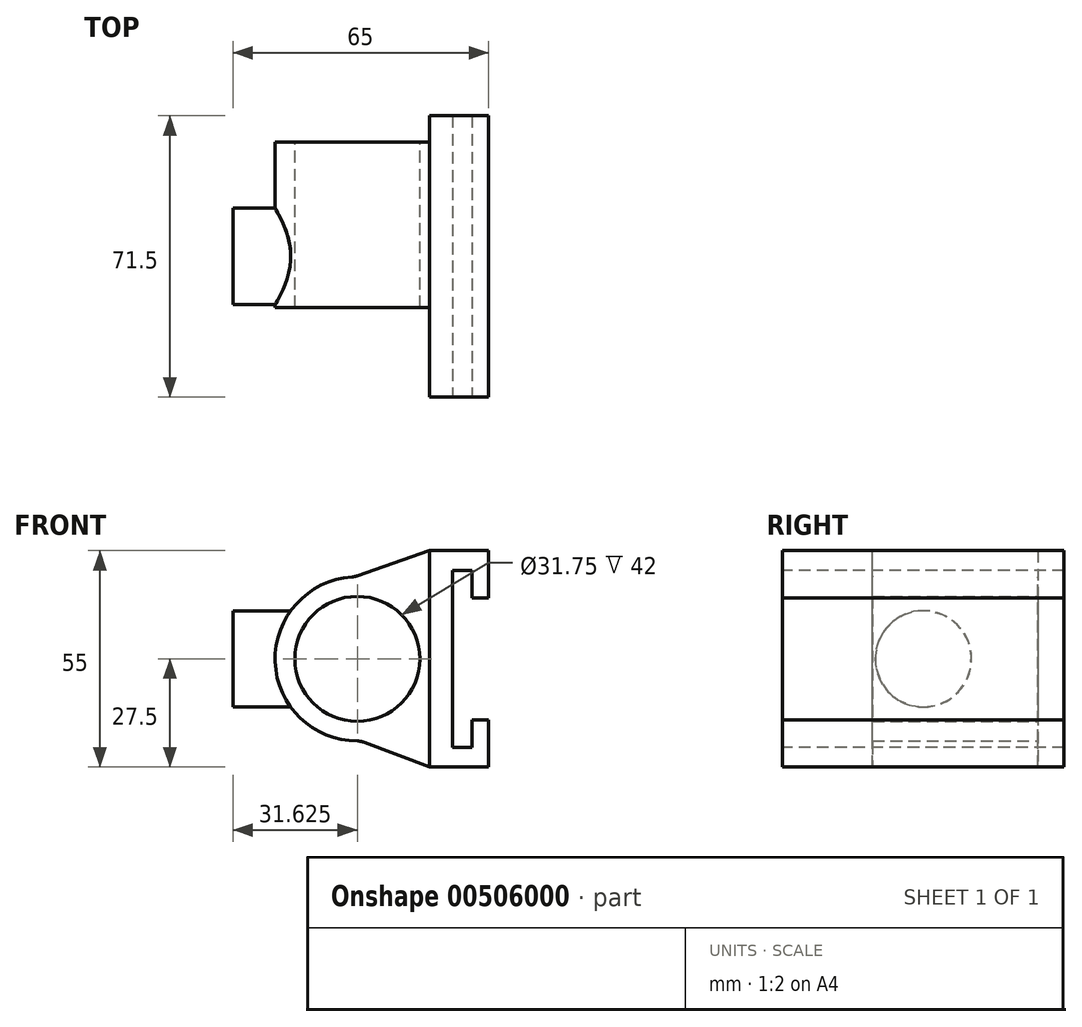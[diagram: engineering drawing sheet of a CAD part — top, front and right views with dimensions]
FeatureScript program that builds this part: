
annotation { "Feature Type Name" : "Feature", "Feature Type Description" : "" }
export const myFeature = defineFeature(function(context is Context, id is Id, definition is map)
    precondition{}
    {
        {
            var Q0;
            Q0=qCreatedBy(makeId("Front.planeOp"),FACE);
            var sketch = newSketch(context, id + "F0", { "sketchPlane" : qUnion([Q0])});
            skLineSegment(sketch, "E0", {"start": v(0, 0) * mm, "end": v(0, 7) * mm});
            skLineSegment(sketch, "E1", {"start": v(0, 0) * mm, "end": v(4.25, 0) * mm});
            skLineSegment(sketch, "E2", {"start": v(4.25, 0) * mm, "end": v(4.25, 12) * mm});
            skLineSegment(sketch, "E3", {"start": v(4.25, 12) * mm, "end": v(-10.75, 12) * mm});
            skLineSegment(sketch, "E4", {"start": v(-10.75, 12) * mm, "end": v(-10.75, -30) * mm});
            skLineSegment(sketch, "E5", {"start": v(-10.75, 12) * mm, "end": v(-10.75, -9) * mm});
            skLineSegment(sketch, "E6.MirrorCS", {"start": v(4.25, -43) * mm, "end": v(-10.75, -43) * mm});
            skLineSegment(sketch, "E7.MirrorCS", {"start": v(0, -31) * mm, "end": v(4.25, -31) * mm});
            skLineSegment(sketch, "E8.MirrorCS", {"start": v(4.25, -31) * mm, "end": v(4.25, -43) * mm});
            skLineSegment(sketch, "E9", {"start": v(-4, -25) * mm, "end": v(-4, 7) * mm});
            skLineSegment(sketch, "E10", {"start": v(-4, 7) * mm, "end": v(0, 7) * mm});
            skLineSegment(sketch, "E11", {"start": v(-10.75, -30) * mm, "end": v(-10.75, -43) * mm});
            skLineSegment(sketch, "E12", {"start": v(-4, -25) * mm, "end": v(-4, -31) * mm});
            skLineSegment(sketch, "E13", {"start": v(0, -31) * mm, "end": v(0, -38) * mm});
            skLineSegment(sketch, "E14", {"start": v(0, -38) * mm, "end": v(-4, -38) * mm});
            skLineSegment(sketch, "E15", {"start": v(-4, -38) * mm, "end": v(-4, -31) * mm});
            skSolve(sketch);
        }
        {
            var Q0;
            Q0 = qSketchRegion(id + "F0", true);
            extrude(context, id + "F1", {"entities" : qUnion([Q0]), "depth" : 71.5 * mm, "offsetDistance" : 25 * mm});
        }
        {
            var Q0;
            Q0=makeQuery(id+"F1.opExtrude","CAP_FACE",FACE,{"disambiguationData":[OSD([sQuery(id+"F0.wireOp",EDGE,"E0"),sQuery(id+"F0.wireOp",EDGE,"E1"),sQuery(id+"F0.wireOp",EDGE,"E2"),sQuery(id+"F0.wireOp",EDGE,"E3"),sQuery(id+"F0.wireOp",EDGE,"E4"),sQuery(id+"F0.wireOp",EDGE,"E5"),sQuery(id+"F0.wireOp",EDGE,"E6.MirrorCS"),sQuery(id+"F0.wireOp",EDGE,"E7.MirrorCS"),sQuery(id+"F0.wireOp",EDGE,"E8.MirrorCS"),sQuery(id+"F0.wireOp",EDGE,"E9"),sQuery(id+"F0.wireOp",EDGE,"E10"),sQuery(id+"F0.wireOp",EDGE,"E11"),sQuery(id+"F0.wireOp",EDGE,"E12"),sQuery(id+"F0.wireOp",EDGE,"E13"),sQuery(id+"F0.wireOp",EDGE,"E14"),sQuery(id+"F0.wireOp",EDGE,"E15")])],"isStart":false});
            var sketch = newSketch(context, id + "F2", { "sketchPlane" : qUnion([Q0])});
            skLineSegment(sketch, "E16", {"start": v(-10.75, -15.5) * mm, "end": v(-13.25, -15.5) * mm});
            skPoint(sketch, "E16.endSnap0", {"position": v(-10.75, -15.5) * mm});
            skLineSegment(sketch, "E17", {"start": v(-13.25, -15.5) * mm, "end": v(-29.12, -15.5) * mm});
            skCircle(sketch, "E18", {"center": v(-29.12, -15.5) * mm, "radius": 15.88 * mm});
            skArc(sketch, "E19.0", {"start": v(-29.1, 5.37) * mm, "mid": v(-49.99, -14.8) * mm, "end": v(-30.48, -36.33) * mm});
            skLineSegment(sketch, "E20", {"start": v(-27.31, 5.7) * mm, "end": v(-10.75, 12) * mm});
            skLineSegment(sketch, "E21", {"start": v(-29.17, -36.6) * mm, "end": v(-10.75, -43) * mm});
            skPoint(sketch, "E22.visualSharp", {"position": v(-28.22, 5.36) * mm});
            skArc(sketch, "E22.filletArc", {"start": v(-29.1, 5.37) * mm, "mid": v(-28.2, 5.46) * mm, "end": v(-27.31, 5.7) * mm});
            skPoint(sketch, "E23.visualSharp", {"position": v(-29.84, -36.36) * mm});
            skArc(sketch, "E23.filletArc", {"start": v(-29.17, -36.6) * mm, "mid": v(-29.82, -36.42) * mm, "end": v(-30.48, -36.33) * mm});
            skSolve(sketch);
        }
        {
            var Q0;
            Q0=makeQuery(id+"F2.imprint","IMPRINT",FACE,{"disambiguationData":[TD([[makeQuery(id+"F2.imprint","IMPRINT",EDGE,{"derivedFrom":sQuery(id+"F2.wireOp",EDGE,"E18")}),-1.0]])]});
            extrude(context, id + "F3", {"entities" : qUnion([Q0]), "operationType" : NewBodyOperationType.ADD, "oppositeDirection" : true, "depth" : 25 * mm, "offsetDistance" : 25 * mm});
        }
        {
            var Q0;
            Q0=makeQuery(id+"F1.opExtrude","SWEPT_BODY",BODY,{"disambiguationData":[OSD([sQuery(id+"F0.wireOp",EDGE,"E0"),sQuery(id+"F0.wireOp",EDGE,"E1"),sQuery(id+"F0.wireOp",EDGE,"E2"),sQuery(id+"F0.wireOp",EDGE,"E3"),sQuery(id+"F0.wireOp",EDGE,"E4"),sQuery(id+"F0.wireOp",EDGE,"E5"),sQuery(id+"F0.wireOp",EDGE,"E6.MirrorCS"),sQuery(id+"F0.wireOp",EDGE,"E7.MirrorCS"),sQuery(id+"F0.wireOp",EDGE,"E8.MirrorCS"),sQuery(id+"F0.wireOp",EDGE,"E9"),sQuery(id+"F0.wireOp",EDGE,"E10"),sQuery(id+"F0.wireOp",EDGE,"E11"),sQuery(id+"F0.wireOp",EDGE,"E12"),sQuery(id+"F0.wireOp",EDGE,"E13"),sQuery(id+"F0.wireOp",EDGE,"E14"),sQuery(id+"F0.wireOp",EDGE,"E15")])]});
            var Q1;
            Q1=makeQuery(id+"F1.opExtrude","CAP_EDGE",EDGE,{"disambiguationData":[OSD([sQuery(id+"F0.wireOp",EDGE,"E3")])],"isStart":true});
            transform(context, id + "F4", {"entities" : qUnion([Q0]), "transformType" : TransformType.ROTATION, "transformAxis" : qUnion([Q1]), "angle" : 180 * degree, "makeCopy" : false});
        }
        {
            var Q0;
            Q0=makeQuery(id+"F3.opExtrude","CAP_FACE",FACE,{"disambiguationData":[OSD([sQuery(id+"F0.wireOp",EDGE,"E4"),sQuery(id+"F0.wireOp",EDGE,"E5"),sQuery(id+"F0.wireOp",EDGE,"E11"),sQuery(id+"F2.wireOp",EDGE,"E18"),sQuery(id+"F2.wireOp",EDGE,"E19.0"),sQuery(id+"F2.wireOp",EDGE,"E20"),sQuery(id+"F2.wireOp",EDGE,"E21"),sQuery(id+"F2.wireOp",EDGE,"E22.filletArc"),sQuery(id+"F2.wireOp",EDGE,"E23.filletArc")])],"isStart":false});
            extrude(context, id + "F5", {"entities" : qUnion([Q0]), "operationType" : NewBodyOperationType.ADD, "depth" : 6.7 * mm, "offsetDistance" : 25 * mm});
        }
        {
            var Q0;
            {var subQ0=sQuery(id+"F0.wireOp",EDGE,"E11");var subQ1=sQuery(id+"F0.wireOp",EDGE,"E5");var subQ2=sQuery(id+"F0.wireOp",EDGE,"E4");Q0=makeQuery(id+"F3.boolean.opBoolean","MERGE",FACE,{"derivedFrom":[makeQuery(id+"F1.opExtrude","CAP_FACE",FACE,{"disambiguationData":[OSD([sQuery(id+"F0.wireOp",EDGE,"E0"),sQuery(id+"F0.wireOp",EDGE,"E1"),sQuery(id+"F0.wireOp",EDGE,"E2"),sQuery(id+"F0.wireOp",EDGE,"E3"),subQ2,subQ1,sQuery(id+"F0.wireOp",EDGE,"E6.MirrorCS"),sQuery(id+"F0.wireOp",EDGE,"E7.MirrorCS"),sQuery(id+"F0.wireOp",EDGE,"E8.MirrorCS"),sQuery(id+"F0.wireOp",EDGE,"E9"),sQuery(id+"F0.wireOp",EDGE,"E10"),subQ0,sQuery(id+"F0.wireOp",EDGE,"E12"),sQuery(id+"F0.wireOp",EDGE,"E13"),sQuery(id+"F0.wireOp",EDGE,"E14"),sQuery(id+"F0.wireOp",EDGE,"E15")])],"isStart":false}),makeQuery(id+"F3.opExtrude","CAP_FACE",FACE,{"disambiguationData":[OSD([subQ2,subQ1,subQ0,sQuery(id+"F2.wireOp",EDGE,"E18"),sQuery(id+"F2.wireOp",EDGE,"E19.0"),sQuery(id+"F2.wireOp",EDGE,"E20"),sQuery(id+"F2.wireOp",EDGE,"E21"),sQuery(id+"F2.wireOp",EDGE,"E22.filletArc"),sQuery(id+"F2.wireOp",EDGE,"E23.filletArc")])],"isStart":true})]});}
            var sketch = newSketch(context, id + "F6", { "sketchPlane" : qUnion([Q0])});
            skLineSegment(sketch, "E24.bottom", {"start": v(10.75, 67) * mm, "end": v(64.25, 67) * mm});
            skLineSegment(sketch, "E24.top", {"start": v(10.75, 8.58) * mm, "end": v(64.25, 8.58) * mm});
            skLineSegment(sketch, "E24.left", {"start": v(10.75, 67) * mm, "end": v(10.75, 8.58) * mm});
            skLineSegment(sketch, "E24.right", {"start": v(64.25, 67) * mm, "end": v(64.25, 8.58) * mm});
            skSolve(sketch);
        }
        {
            var Q0;
            Q0 = qSketchRegion(id + "F6", true);
            extrude(context, id + "F7", {"entities" : qUnion([Q0]), "operationType" : NewBodyOperationType.REMOVE, "oppositeDirection" : true, "depth" : 6.7 * mm, "offsetDistance" : 25 * mm});
        }
        {
            var Q0;
            Q0=makeQuery(id+"F1.opExtrude","SWEPT_FACE",FACE,{"disambiguationData":[OSD([sQuery(id+"F0.wireOp",EDGE,"E4"),sQuery(id+"F0.wireOp",EDGE,"E5"),sQuery(id+"F0.wireOp",EDGE,"E11")])]});
            var sketch = newSketch(context, id + "F8", { "sketchPlane" : qUnion([Q0])});
            skCircle(sketch, "E25", {"center": v(-35.75, 39.5) * mm, "radius": 12.25 * mm});
            skSolve(sketch);
        }
        {
            var Q0;
            Q0=makeQuery(id+"F5.opExtrude","CAP_FACE",FACE,{"disambiguationData":[OSD([sQuery(id+"F0.wireOp",EDGE,"E4"),sQuery(id+"F0.wireOp",EDGE,"E5"),sQuery(id+"F0.wireOp",EDGE,"E11"),sQuery(id+"F2.wireOp",EDGE,"E18"),sQuery(id+"F2.wireOp",EDGE,"E19.0"),sQuery(id+"F2.wireOp",EDGE,"E20"),sQuery(id+"F2.wireOp",EDGE,"E21"),sQuery(id+"F2.wireOp",EDGE,"E22.filletArc"),sQuery(id+"F2.wireOp",EDGE,"E23.filletArc")])],"isStart":false});
            extrude(context, id + "F9", {"entities" : qUnion([Q0]), "operationType" : NewBodyOperationType.ADD, "depth" : 17 * mm, "offsetDistance" : 25 * mm});
        }
        {
            var Q0;
            Q0 = qSketchRegion(id + "F8", true);
            var Q1;
            Q1=sQuery(id+"F8.wireOp",EDGE,"E25");
            extrude(context, id + "F10", {"entities" : qUnion([Q0]), "operationType" : NewBodyOperationType.ADD, "surfaceEntities" : qUnion([Q1]), "depth" : 50 * mm, "offsetDistance" : 25 * mm});
        }
        {
            var Q0;
            Q0=makeQuery(id+"F7.boolean.opBoolean","COPY",FACE,{"derivedFrom":makeQuery(id+"F7.opExtrude","CAP_FACE",FACE,{"disambiguationData":[OSD([sQuery(id+"F6.wireOp",EDGE,"E24.bottom"),sQuery(id+"F6.wireOp",EDGE,"E24.top"),sQuery(id+"F6.wireOp",EDGE,"E24.left"),sQuery(id+"F6.wireOp",EDGE,"E24.right")])],"isStart":false})});
            var sketch = newSketch(context, id + "F11", { "sketchPlane" : qUnion([Q0])});
            skCircle(sketch, "E26", {"center": v(29.12, 39.5) * mm, "radius": 15.88 * mm});
            skSolve(sketch);
        }
        {
            var Q0;
            Q0=makeQuery(id+"F11.imprint","IMPRINT",FACE,{"disambiguationData":[TD([[makeQuery(id+"F11.imprint","IMPRINT",EDGE,{"derivedFrom":sQuery(id+"F11.wireOp",EDGE,"E26")}),-1.0]])]});
            var Q1;
            Q1=sQuery(id+"F11.wireOp",EDGE,"E26");
            extrude(context, id + "F12", {"entities" : qUnion([Q0]), "operationType" : NewBodyOperationType.REMOVE, "surfaceEntities" : qUnion([Q1]), "oppositeDirection" : true, "depth" : 100 * mm, "offsetDistance" : 25 * mm});
        }
        {
            var Q0;
            Q0=makeQuery(id+"F1.opExtrude","SWEPT_FACE",FACE,{"disambiguationData":[OSD([sQuery(id+"F0.wireOp",EDGE,"E9"),sQuery(id+"F0.wireOp",EDGE,"E12"),sQuery(id+"F0.wireOp",EDGE,"E15")])]});
            extrude(context, id + "F13", {"entities" : qUnion([Q0]), "operationType" : NewBodyOperationType.REMOVE, "oppositeDirection" : true, "depth" : 1 * mm, "offsetDistance" : 25 * mm});
        }
    });
